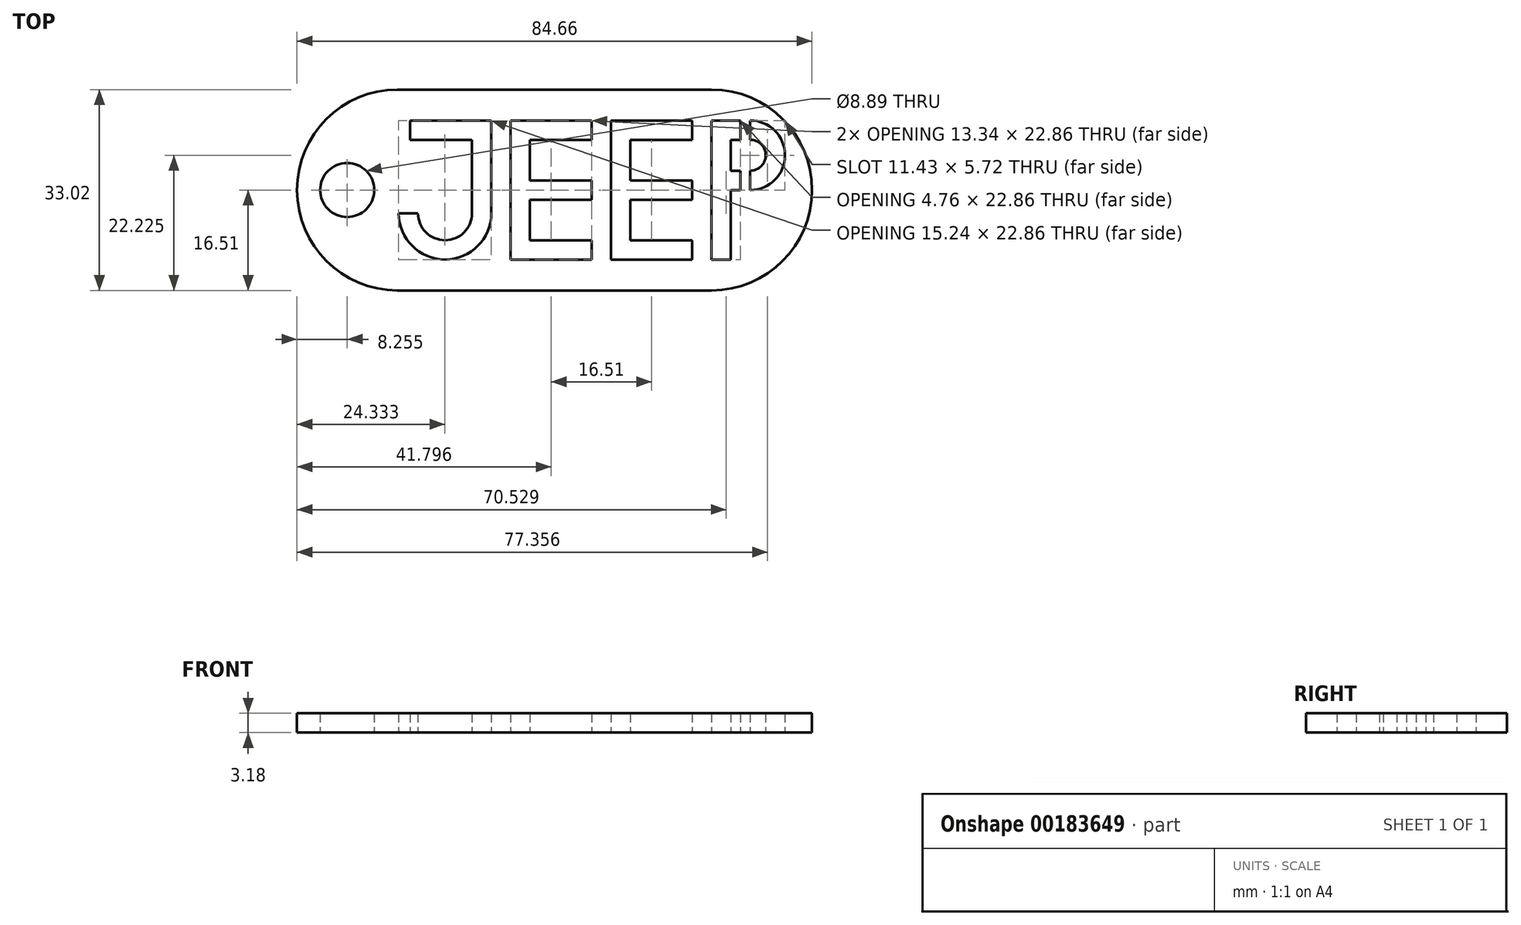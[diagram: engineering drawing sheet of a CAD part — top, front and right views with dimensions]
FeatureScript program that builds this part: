
annotation { "Feature Type Name" : "Feature", "Feature Type Description" : "" }
export const myFeature = defineFeature(function(context is Context, id is Id, definition is map)
    precondition{}
    {
        {
            var Q0;
            Q0=qCreatedBy(makeId("Top.planeOp"),FACE);
            var sketch = newSketch(context, id + "F0", { "sketchPlane" : qUnion([Q0])});
            skLineSegment(sketch, "E0.bottom", {"start": v(0, 0) * mm, "end": v(84.66, 0) * mm, "construction": true});
            skLineSegment(sketch, "E0.top", {"start": v(0, 33.02) * mm, "end": v(84.66, 33.02) * mm, "construction": true});
            skLineSegment(sketch, "E0.left", {"start": v(0, 0) * mm, "end": v(0, 33.02) * mm, "construction": true});
            skLineSegment(sketch, "E0.right", {"start": v(84.66, 0) * mm, "end": v(84.66, 33.02) * mm, "construction": true});
            skCircle(sketch, "E1", {"center": v(16.51, 16.51) * mm, "radius": 16.51 * mm, "construction": true});
            skCircle(sketch, "E2", {"center": v(68.15, 16.51) * mm, "radius": 16.51 * mm, "construction": true});
            skArc(sketch, "E3", {"start": v(16.51, 33.02) * mm, "mid": v(0, 16.5) * mm, "end": v(16.51, 0) * mm});
            skArc(sketch, "E4", {"start": v(68.15, 0) * mm, "mid": v(84.66, 16.51) * mm, "end": v(68.15, 33.02) * mm});
            skLineSegment(sketch, "E5", {"start": v(68.15, 0) * mm, "end": v(16.51, 0) * mm});
            skCircle(sketch, "E6", {"center": v(8.26, 16.51) * mm, "radius": 4.45 * mm});
            skLineSegment(sketch, "E7", {"start": v(16.51, 16.51) * mm, "end": v(0, 16.51) * mm, "construction": true});
            skLineSegment(sketch, "E8", {"start": v(16.51, 33.02) * mm, "end": v(30.48, 33.02) * mm});
            skLineSegment(sketch, "E9", {"start": v(68.15, 33.02) * mm, "end": v(30.48, 33.02) * mm});
            skLineSegment(sketch, "E10", {"start": v(16.51, 33.02) * mm, "end": v(16.51, 0) * mm, "construction": true});
            skLineSegment(sketch, "E11", {"start": v(30.48, 33.02) * mm, "end": v(30.48, 27.94) * mm, "construction": true});
            skLineSegment(sketch, "E12", {"start": v(30.6, 0) * mm, "end": v(30.6, 5.08) * mm, "construction": true});
            skLineSegment(sketch, "E13", {"start": v(30.48, 27.94) * mm, "end": v(16.51, 27.94) * mm, "construction": true});
            skLineSegment(sketch, "E14", {"start": v(30.6, 5.08) * mm, "end": v(16.51, 5.08) * mm, "construction": true});
            skLineSegment(sketch, "E15", {"start": v(30.6, 5.08) * mm, "end": v(84.66, 5.08) * mm, "construction": true});
            skLineSegment(sketch, "E16", {"start": v(84.66, 16.51) * mm, "end": v(81.48, 16.51) * mm, "construction": true});
            skLineSegment(sketch, "E17", {"start": v(81.48, 16.51) * mm, "end": v(81.48, 27.94) * mm, "construction": true});
            skLineSegment(sketch, "E18", {"start": v(81.48, 16.51) * mm, "end": v(81.48, 5.08) * mm, "construction": true});
            skLineSegment(sketch, "E19", {"start": v(68.15, 16.51) * mm, "end": v(64.97, 16.51) * mm, "construction": true});
            skLineSegment(sketch, "E20", {"start": v(64.97, 16.51) * mm, "end": v(51.64, 16.51) * mm, "construction": true});
            skLineSegment(sketch, "E21", {"start": v(51.64, 16.51) * mm, "end": v(48.46, 16.51) * mm, "construction": true});
            skLineSegment(sketch, "E22", {"start": v(48.46, 16.51) * mm, "end": v(35.13, 16.51) * mm, "construction": true});
            skLineSegment(sketch, "E23", {"start": v(35.13, 16.51) * mm, "end": v(31.95, 16.51) * mm, "construction": true});
            skLineSegment(sketch, "E24", {"start": v(31.95, 16.51) * mm, "end": v(18.62, 16.51) * mm, "construction": true});
            skLineSegment(sketch, "E25", {"start": v(18.62, 5.08) * mm, "end": v(18.62, 27.94) * mm, "construction": true});
            skLineSegment(sketch, "E26", {"start": v(31.95, 5.08) * mm, "end": v(31.95, 27.94) * mm, "construction": true});
            skLineSegment(sketch, "E27", {"start": v(35.13, 5.08) * mm, "end": v(35.13, 27.94) * mm, "construction": true});
            skLineSegment(sketch, "E28", {"start": v(48.46, 27.94) * mm, "end": v(48.46, 5.08) * mm, "construction": true});
            skLineSegment(sketch, "E29", {"start": v(51.64, 27.94) * mm, "end": v(51.64, 5.08) * mm, "construction": true});
            skLineSegment(sketch, "E30", {"start": v(64.97, 5.08) * mm, "end": v(64.97, 27.94) * mm, "construction": true});
            skLineSegment(sketch, "E31", {"start": v(68.15, 5.08) * mm, "end": v(68.15, 27.94) * mm, "construction": true});
            skLineSegment(sketch, "E32", {"start": v(18.62, 27.94) * mm, "end": v(31.95, 27.94) * mm});
            skLineSegment(sketch, "E33", {"start": v(31.95, 27.94) * mm, "end": v(31.95, 24.77) * mm});
            skLineSegment(sketch, "E34", {"start": v(18.62, 27.94) * mm, "end": v(18.62, 24.77) * mm});
            skLineSegment(sketch, "E35", {"start": v(18.62, 24.77) * mm, "end": v(28.78, 24.77) * mm});
            skLineSegment(sketch, "E36", {"start": v(31.95, 24.77) * mm, "end": v(31.95, 24.77) * mm});
            skLineSegment(sketch, "E37", {"start": v(31.95, 24.77) * mm, "end": v(31.95, 12.7) * mm});
            skLineSegment(sketch, "E38", {"start": v(48.46, 27.94) * mm, "end": v(35.13, 27.94) * mm});
            skLineSegment(sketch, "E39", {"start": v(48.46, 27.94) * mm, "end": v(48.46, 24.77) * mm});
            skLineSegment(sketch, "E40", {"start": v(48.46, 24.77) * mm, "end": v(38.3, 24.77) * mm});
            skLineSegment(sketch, "E41", {"start": v(35.13, 27.94) * mm, "end": v(35.13, 5.08) * mm});
            skLineSegment(sketch, "E42", {"start": v(35.13, 5.08) * mm, "end": v(48.46, 5.08) * mm});
            skLineSegment(sketch, "E43", {"start": v(48.46, 5.08) * mm, "end": v(48.46, 8.26) * mm});
            skLineSegment(sketch, "E44", {"start": v(48.46, 8.26) * mm, "end": v(38.3, 8.26) * mm});
            skLineSegment(sketch, "E45", {"start": v(38.3, 24.77) * mm, "end": v(38.3, 18.1) * mm});
            skLineSegment(sketch, "E46", {"start": v(38.3, 18.1) * mm, "end": v(48.46, 18.1) * mm});
            skLineSegment(sketch, "E47", {"start": v(48.46, 18.1) * mm, "end": v(48.46, 14.92) * mm});
            skLineSegment(sketch, "E48", {"start": v(48.46, 14.92) * mm, "end": v(38.3, 14.92) * mm});
            skLineSegment(sketch, "E49", {"start": v(38.3, 14.92) * mm, "end": v(38.3, 8.26) * mm});
            skLineSegment(sketch, "E50", {"start": v(64.97, 24.77) * mm, "end": v(64.97, 27.94) * mm});
            skLineSegment(sketch, "E51", {"start": v(64.97, 27.94) * mm, "end": v(51.64, 27.94) * mm});
            skLineSegment(sketch, "E52", {"start": v(51.64, 27.94) * mm, "end": v(51.64, 5.08) * mm});
            skLineSegment(sketch, "E53", {"start": v(51.64, 5.08) * mm, "end": v(64.97, 5.08) * mm});
            skLineSegment(sketch, "E54", {"start": v(64.97, 5.08) * mm, "end": v(64.97, 8.26) * mm});
            skLineSegment(sketch, "E55", {"start": v(64.97, 8.26) * mm, "end": v(54.81, 8.26) * mm});
            skLineSegment(sketch, "E56", {"start": v(54.81, 8.26) * mm, "end": v(54.81, 14.92) * mm});
            skPoint(sketch, "E56.endSnap0", {"position": v(43.38, 14.92) * mm});
            skLineSegment(sketch, "E57", {"start": v(54.81, 14.92) * mm, "end": v(64.97, 14.92) * mm});
            skLineSegment(sketch, "E58", {"start": v(64.97, 14.92) * mm, "end": v(64.97, 18.1) * mm});
            skLineSegment(sketch, "E59", {"start": v(64.97, 18.1) * mm, "end": v(54.81, 18.1) * mm});
            skLineSegment(sketch, "E60", {"start": v(54.81, 18.1) * mm, "end": v(54.81, 24.77) * mm});
            skLineSegment(sketch, "E61", {"start": v(54.81, 24.77) * mm, "end": v(64.97, 24.77) * mm});
            skLineSegment(sketch, "E62", {"start": v(31.95, 12.7) * mm, "end": v(28.78, 12.7) * mm, "construction": true});
            skLineSegment(sketch, "E63", {"start": v(28.78, 24.77) * mm, "end": v(28.78, 12.7) * mm});
            skArc(sketch, "E64", {"start": v(16.71, 12.7) * mm, "mid": v(24.33, 5.08) * mm, "end": v(31.95, 12.7) * mm});
            skArc(sketch, "E65", {"start": v(19.89, 12.7) * mm, "mid": v(24.33, 8.26) * mm, "end": v(28.78, 12.7) * mm});
            skLineSegment(sketch, "E66", {"start": v(16.71, 12.7) * mm, "end": v(19.89, 12.7) * mm});
            skLineSegment(sketch, "E67", {"start": v(68.15, 27.94) * mm, "end": v(68.15, 5.08) * mm});
            skLineSegment(sketch, "E68", {"start": v(68.15, 5.08) * mm, "end": v(71.32, 5.08) * mm});
            skArc(sketch, "E69", {"start": v(74.5, 16.51) * mm, "mid": v(80.21, 22.23) * mm, "end": v(74.5, 27.94) * mm});
            skLineSegment(sketch, "E70", {"start": v(74.5, 27.94) * mm, "end": v(74.5, 24.77) * mm});
            skArc(sketch, "E71", {"start": v(74.5, 19.69) * mm, "mid": v(77.04, 22.23) * mm, "end": v(74.5, 24.77) * mm});
            skLineSegment(sketch, "E72", {"start": v(71.32, 5.08) * mm, "end": v(71.32, 16.51) * mm});
            skLineSegment(sketch, "E73", {"start": v(71.32, 24.77) * mm, "end": v(71.32, 19.69) * mm});
            skLineSegment(sketch, "E74", {"start": v(74.5, 27.94) * mm, "end": v(72.91, 27.94) * mm, "construction": true});
            skLineSegment(sketch, "E75", {"start": v(68.15, 27.94) * mm, "end": v(72.91, 27.94) * mm});
            skLineSegment(sketch, "E76", {"start": v(72.91, 27.94) * mm, "end": v(72.91, 24.77) * mm});
            skLineSegment(sketch, "E77", {"start": v(71.32, 24.77) * mm, "end": v(72.91, 24.77) * mm});
            skLineSegment(sketch, "E78", {"start": v(71.32, 19.69) * mm, "end": v(72.91, 19.69) * mm});
            skLineSegment(sketch, "E79", {"start": v(71.32, 16.51) * mm, "end": v(72.91, 16.51) * mm});
            skLineSegment(sketch, "E80", {"start": v(72.91, 19.69) * mm, "end": v(72.91, 16.51) * mm});
            skLineSegment(sketch, "E81", {"start": v(74.5, 19.69) * mm, "end": v(74.5, 16.51) * mm});
            skSolve(sketch);
        }
        {
            var Q0;
            Q0=makeQuery(id+"F0.imprint","IMPRINT",FACE,{"disambiguationData":[TD([[makeQuery(id+"F0.imprint","IMPRINT",EDGE,{"derivedFrom":sQuery(id+"F0.wireOp",EDGE,"E3")}),1.0]])]});
            var Q1;
            Q1=makeQuery(id+"F0.imprint","IMPRINT",FACE,{"disambiguationData":[TD([[makeQuery(id+"F0.imprint","IMPRINT",EDGE,{"derivedFrom":sQuery(id+"F0.wireOp",EDGE,"E71")}),1.0]])]});
            extrude(context, id + "F1", {"entities" : qUnion([Q0, Q1]), "depth" : 3.17 * mm});
        }
    });
